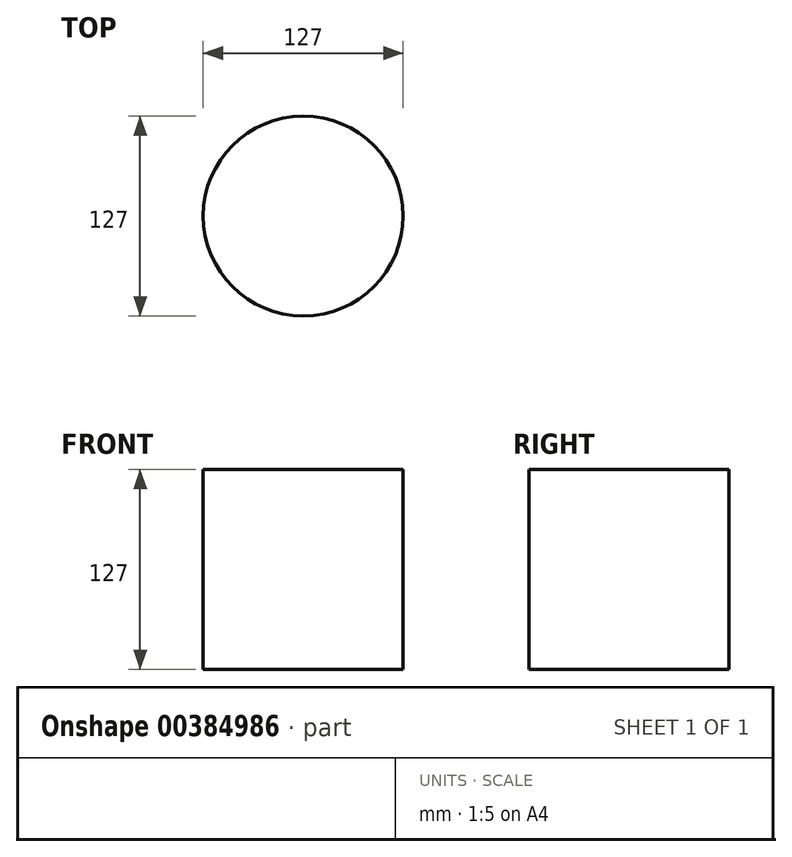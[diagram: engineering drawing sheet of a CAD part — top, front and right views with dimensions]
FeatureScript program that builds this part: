
annotation { "Feature Type Name" : "Feature", "Feature Type Description" : "" }
export const myFeature = defineFeature(function(context is Context, id is Id, definition is map)
    precondition{}
    {
        {
            var Q0;
            Q0=qCreatedBy(makeId("Top.planeOp"),FACE);
            var sketch = newSketch(context, id + "F0", { "sketchPlane" : qUnion([Q0])});
            skCircle(sketch, "E0", {"center": v(0, 0) * mm, "radius": 63.5 * mm});
            skSolve(sketch);
        }
        {
            var Q0;
            Q0 = qSketchRegion(id + "F0", true);
            extrude(context, id + "F1", {"entities" : qUnion([Q0]), "endBound" : BoundingType.SYMMETRIC, "depth" : 127 * mm});
        }
        {
            var Q0;
            Q0=makeQuery(id+"F1.opExtrude","CAP_FACE",FACE,{"disambiguationData":[OSD([sQuery(id+"F0.wireOp",EDGE,"E0")])],"isStart":false});
            var sketch = newSketch(context, id + "F2", { "sketchPlane" : qUnion([Q0])});
            skLineSegment(sketch, "E1", {"start": v(-63.5, 0) * mm, "end": v(63.5, 0) * mm});
            skSolve(sketch);
        }
    });
